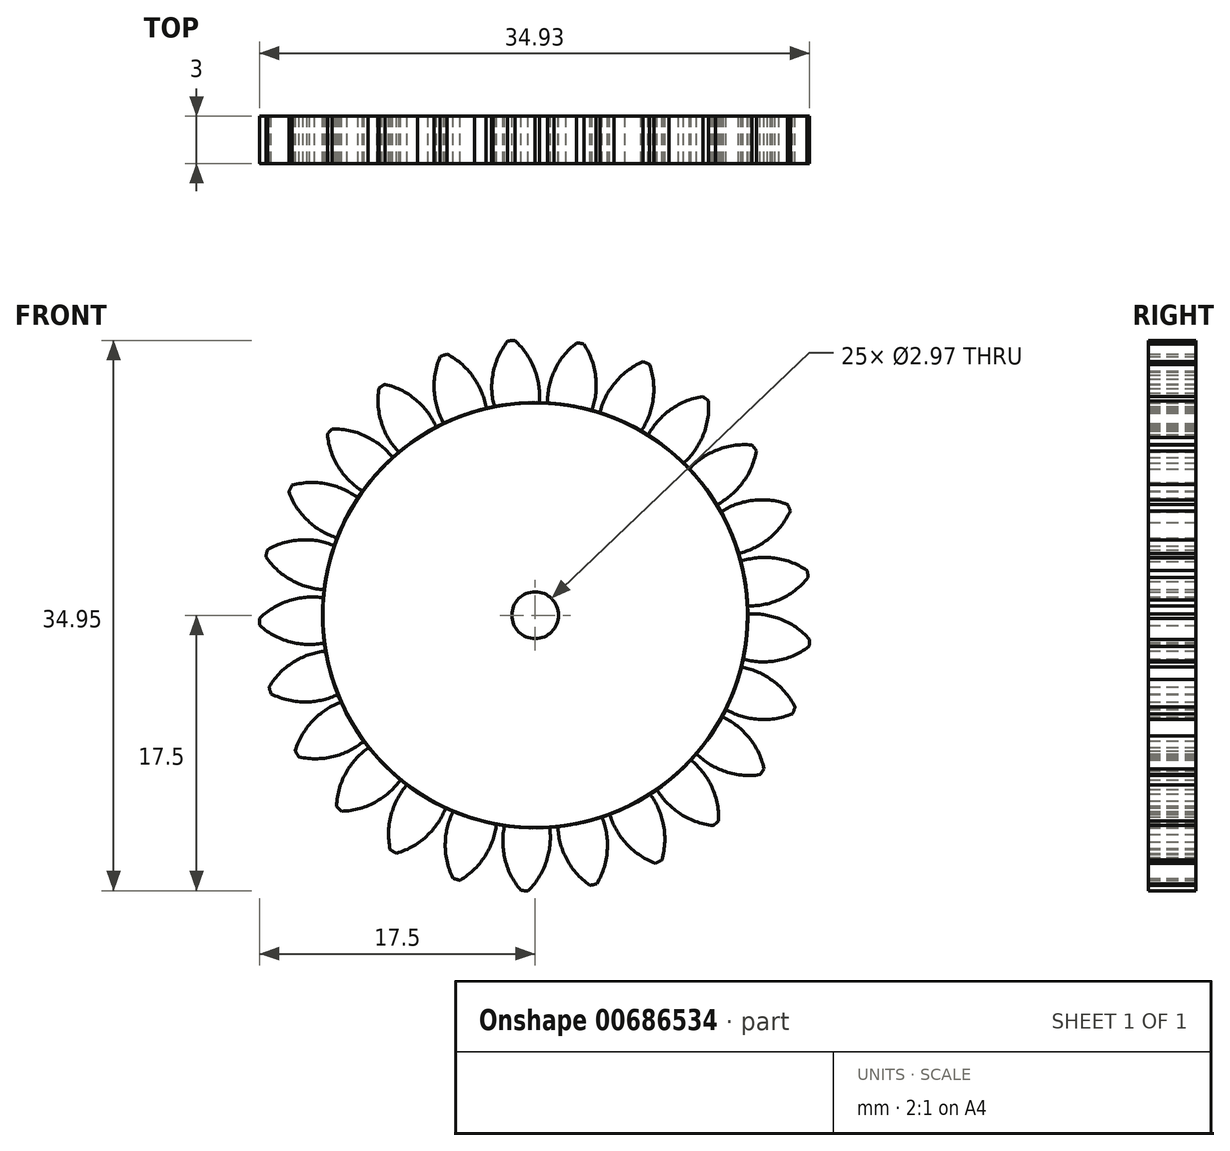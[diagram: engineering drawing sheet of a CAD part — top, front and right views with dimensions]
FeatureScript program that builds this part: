
annotation { "Feature Type Name" : "Feature", "Feature Type Description" : "" }
export const myFeature = defineFeature(function(context is Context, id is Id, definition is map)
    precondition{}
    {
        {
            var Q0;
            Q0=qCreatedBy(makeId("Front.planeOp"),FACE);
            var sketch = newSketch(context, id + "F0", { "sketchPlane" : qUnion([Q0])});
            skCircle(sketch, "E0", {"center": v(0, 0) * mm, "radius": 13.5 * mm});
            skCircle(sketch, "E1", {"center": v(0, 0) * mm, "radius": 17.5 * mm, "construction": true});
            skLineSegment(sketch, "E2", {"start": v(0, 0) * mm, "end": v(-2.86, 32.7) * mm, "construction": true});
            skCircle(sketch, "E3", {"center": v(0, 0) * mm, "radius": 15.5 * mm, "construction": true});
            skLineSegment(sketch, "E4", {"start": v(0, 15.5) * mm, "end": v(-34.56, 15.5) * mm, "construction": true});
            skLineSegment(sketch, "E5", {"start": v(0, 15.5) * mm, "end": v(-34.17, 3.06) * mm, "construction": true});
            skCircle(sketch, "E6", {"center": v(0, 0) * mm, "radius": 14.57 * mm, "construction": true});
            skCircle(sketch, "E7", {"center": v(0, 15.5) * mm, "radius": 5 * mm, "construction": true});
            skArc(sketch, "E8", {"start": v(0, 15.5) * mm, "mid": v(-0.52, 16.56) * mm, "end": v(-1.3, 17.45) * mm});
            skArc(sketch, "E9", {"start": v(0.26, 13.5) * mm, "mid": v(0.24, 14.51) * mm, "end": v(0, 15.5) * mm});
            skArc(sketch, "E10.MirrorCS", {"start": v(-2.7, 15.26) * mm, "mid": v(-2.36, 16.4) * mm, "end": v(-1.75, 17.41) * mm});
            skArc(sketch, "E11.MirrorCS", {"start": v(-2.6, 13.25) * mm, "mid": v(-2.75, 14.25) * mm, "end": v(-2.7, 15.26) * mm});
            skArc(sketch, "E12", {"start": v(-1.3, 17.45) * mm, "mid": v(-1.53, 17.44) * mm, "end": v(-1.75, 17.41) * mm});
            skCircle(sketch, "E13", {"center": v(0, 0) * mm, "radius": 1.49 * mm});
            skSolve(sketch);
        }
        {
            var Q0;
            {var subQ0=sQuery(id+"F0.wireOp",EDGE,"E0");var subQ1=makeQuery(id+"F0.imprint","INTERSECT",VERTEX,{"derivedFrom":[subQ0,sQuery(id+"F0.wireOp",EDGE,"E9")]});Q0=makeQuery(id+"F0.imprint","IMPRINT",FACE,{"disambiguationData":[TD([[makeQuery(id+"F0.imprint","IMPRINT",EDGE,{"disambiguationData":[TD([[subQ1,-1.0]])],"derivedFrom":subQ0}),1.0]])]});}
            var Q1;
            Q1=makeQuery(id+"F0.imprint","IMPRINT",FACE,{"disambiguationData":[TD([[makeQuery(id+"F0.imprint","IMPRINT",EDGE,{"derivedFrom":sQuery(id+"F0.wireOp",EDGE,"E8")}),1.0]])]});
            extrude(context, id + "F1", {"entities" : qUnion([Q0, Q1]), "depth" : 3 * mm, "offsetDistance" : 25 * mm});
        }
        {
            var Q0;
            Q0=makeQuery(id+"F1.opExtrude","SWEPT_BODY",BODY,{"disambiguationData":[OSD([sQuery(id+"F0.wireOp",EDGE,"E0"),sQuery(id+"F0.wireOp",EDGE,"E8"),sQuery(id+"F0.wireOp",EDGE,"E9"),sQuery(id+"F0.wireOp",EDGE,"E10.MirrorCS"),sQuery(id+"F0.wireOp",EDGE,"E11.MirrorCS"),sQuery(id+"F0.wireOp",EDGE,"iEwE1jP1-MdBb-QcpV-rEfn-gcm169mYf5Qv")])]});
            var Q1;
            Q1=makeQuery(id+"F1.opExtrude","SWEPT_FACE",FACE,{"disambiguationData":[OSD([sQuery(id+"F0.wireOp",EDGE,"E0")])]});
            circularPattern(context, id + "F2", {"entities" : qUnion([Q0]), "axis" : qUnion([Q1]), "angle" : 360 * degree, "instanceCount" : 25, "equalSpace" : true});
        }
    });
